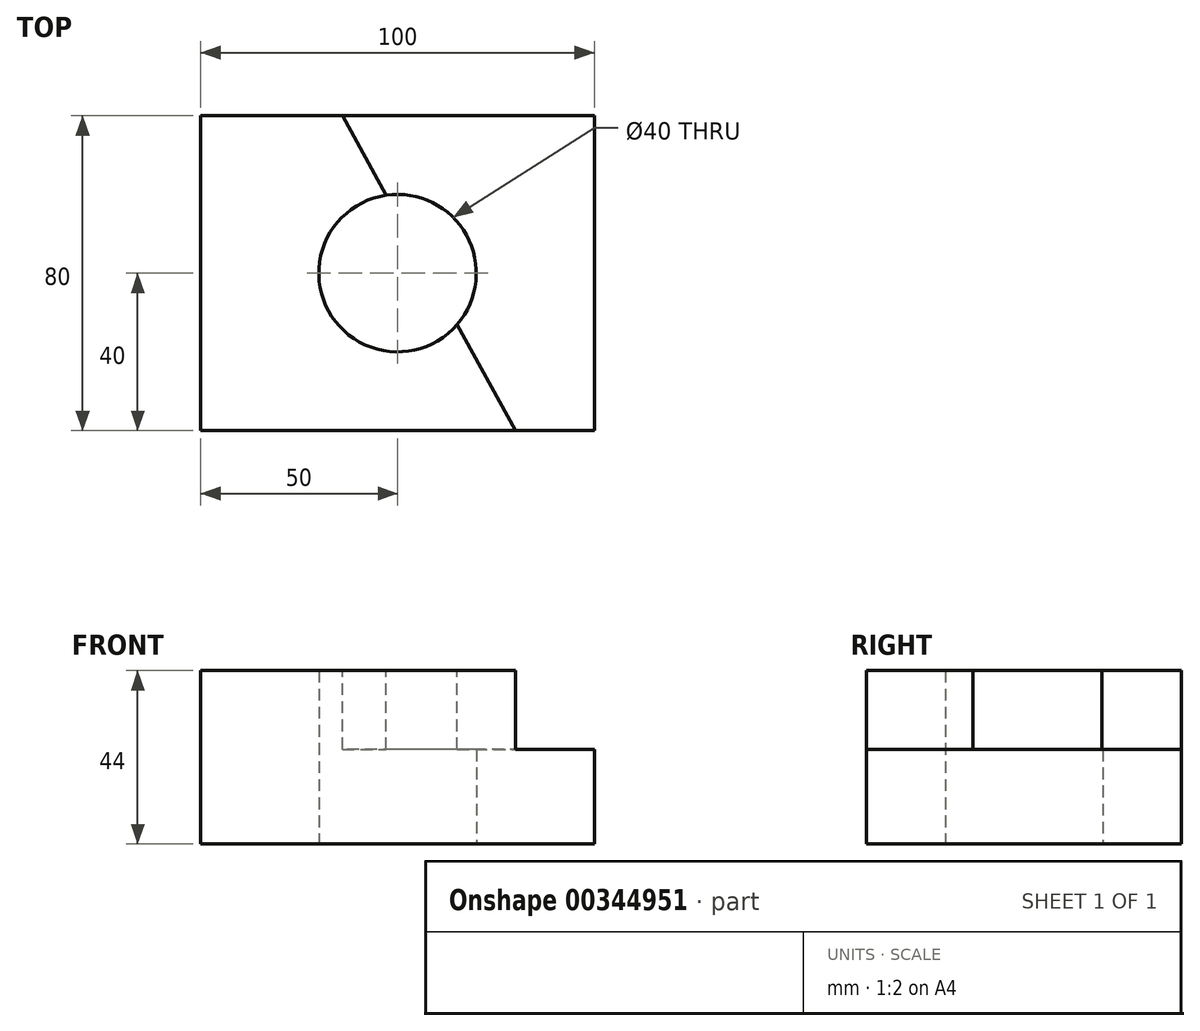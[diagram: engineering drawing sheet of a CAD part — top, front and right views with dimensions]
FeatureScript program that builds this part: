
annotation { "Feature Type Name" : "Feature", "Feature Type Description" : "" }
export const myFeature = defineFeature(function(context is Context, id is Id, definition is map)
    precondition{}
    {
        {
            var Q0;
            Q0=qCreatedBy(makeId("Top.planeOp"),FACE);
            var sketch = newSketch(context, id + "F0", { "sketchPlane" : qUnion([Q0])});
            skLineSegment(sketch, "E0.bottom", {"start": v(50, 40) * mm, "end": v(-50, 40) * mm});
            skLineSegment(sketch, "E0.top", {"start": v(50, -40) * mm, "end": v(-50, -40) * mm});
            skLineSegment(sketch, "E0.left", {"start": v(50, 40) * mm, "end": v(50, -40) * mm});
            skLineSegment(sketch, "E0.right", {"start": v(-50, 40) * mm, "end": v(-50, -40) * mm});
            skPoint(sketch, "E0.middle", {"position": v(0, 0) * mm});
            skCircle(sketch, "E1", {"center": v(0, 0) * mm, "radius": 20 * mm});
            skLineSegment(sketch, "E2", {"start": v(-14, 40) * mm, "end": v(-14, -40) * mm, "construction": true});
            skLineSegment(sketch, "E3", {"start": v(30, 40) * mm, "end": v(30, -40) * mm, "construction": true});
            skLineSegment(sketch, "E4", {"start": v(-14, 40) * mm, "end": v(30, -40) * mm});
            skSolve(sketch);
        }
        {
            var Q0;
            Q0 = qSketchRegion(id + "F0", true);
            extrude(context, id + "F1", {"entities" : qUnion([Q0]), "depth" : 44 * mm});
        }
        {
            var Q0;
            Q0=makeQuery(id+"F1.opExtrude","CAP_FACE",FACE,{"disambiguationData":[OSD([sQuery(id+"F0.wireOp",EDGE,"E0.bottom"),sQuery(id+"F0.wireOp",EDGE,"E0.top"),sQuery(id+"F0.wireOp",EDGE,"E0.left"),sQuery(id+"F0.wireOp",EDGE,"E0.right"),sQuery(id+"F0.wireOp",EDGE,"E1")])],"isStart":false});
            var sketch = newSketch(context, id + "F2", { "sketchPlane" : qUnion([Q0])});
            skLineSegment(sketch, "E5", {"start": v(-14, 40) * mm, "end": v(30, -40) * mm});
            skLineSegment(sketch, "E6.bottom", {"start": v(50, 40) * mm, "end": v(-50, 40) * mm});
            skLineSegment(sketch, "E6.top", {"start": v(50, -40) * mm, "end": v(-50, -40) * mm});
            skLineSegment(sketch, "E6.left", {"start": v(50, 40) * mm, "end": v(50, -40) * mm});
            skLineSegment(sketch, "E6.right", {"start": v(-50, 40) * mm, "end": v(-50, -40) * mm});
            skPoint(sketch, "E6.middle", {"position": v(0, 0) * mm});
            skCircle(sketch, "E7", {"center": v(0, 0) * mm, "radius": 20 * mm});
            skSolve(sketch);
        }
        {
            var Q0;
            {var subQ0=sQuery(id+"F2.wireOp",EDGE,"E6.left");Q0=makeQuery(id+"F2.imprint","IMPRINT",FACE,{"disambiguationData":[TD([[makeQuery(id+"F2.imprint","IMPRINT",EDGE,{"derivedFrom":subQ0}),-1.0]])]});}
            extrude(context, id + "F3", {"entities" : qUnion([Q0]), "operationType" : NewBodyOperationType.REMOVE, "oppositeDirection" : true, "depth" : 20 * mm});
        }
    });
